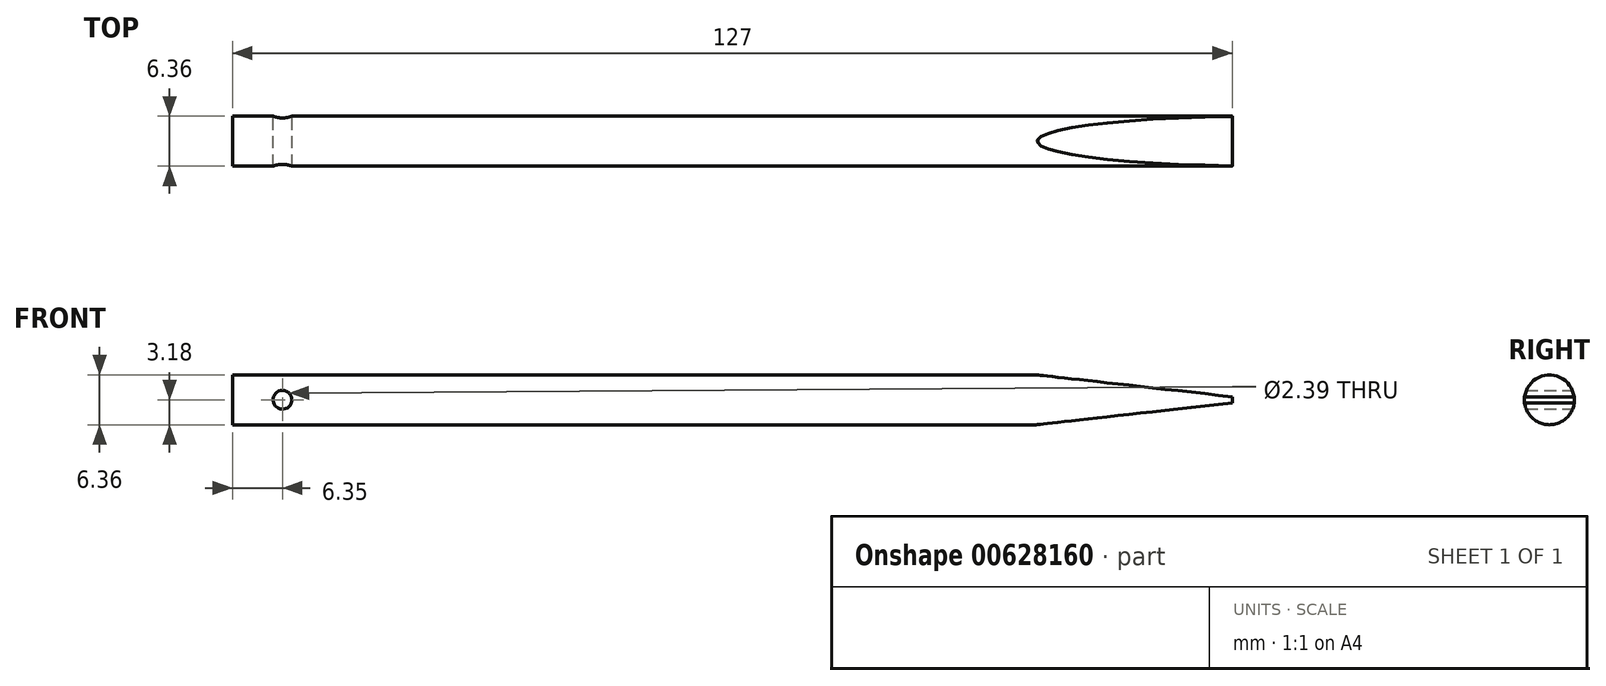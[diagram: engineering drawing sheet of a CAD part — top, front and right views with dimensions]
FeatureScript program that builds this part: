
annotation { "Feature Type Name" : "Feature", "Feature Type Description" : "" }
export const myFeature = defineFeature(function(context is Context, id is Id, definition is map)
    precondition{}
    {
        {
            var Q0;
            Q0=qCreatedBy(makeId("Right.planeOp"),FACE);
            var sketch = newSketch(context, id + "F0", { "sketchPlane" : qUnion([Q0])});
            skCircle(sketch, "E0", {"center": v(0, 0) * mm, "radius": 3.18 * mm});
            skSolve(sketch);
        }
        {
            var Q0;
            Q0 = qSketchRegion(id + "F0", true);
            extrude(context, id + "F1", {"entities" : qUnion([Q0]), "oppositeDirection" : true, "depth" : 127 * mm, "offsetDistance" : 25.4 * mm});
        }
        {
            var Q0;
            Q0=qCreatedBy(makeId("Front.planeOp"),FACE);
            var sketch = newSketch(context, id + "F2", { "sketchPlane" : qUnion([Q0])});
            skLineSegment(sketch, "E1", {"start": v(0, 0) * mm, "end": v(-25.4, 0) * mm, "construction": true});
            skLineSegment(sketch, "E2", {"start": v(0, 0) * mm, "end": v(0, 0.38) * mm});
            skLineSegment(sketch, "E3", {"start": v(-25.4, 3.23) * mm, "end": v(0, 0.38) * mm});
            skLineSegment(sketch, "E4.MirrorCS", {"start": v(0, 0) * mm, "end": v(0, -0.38) * mm});
            skLineSegment(sketch, "E5.MirrorCS", {"start": v(-25.4, -3.23) * mm, "end": v(0, -0.38) * mm});
            skLineSegment(sketch, "E6", {"start": v(-25.4, 3.23) * mm, "end": v(0, 3.23) * mm});
            skLineSegment(sketch, "E7", {"start": v(0, 3.23) * mm, "end": v(0, 0.38) * mm});
            skLineSegment(sketch, "E8", {"start": v(0, -0.38) * mm, "end": v(0, -3.21) * mm});
            skLineSegment(sketch, "E9", {"start": v(0, -3.21) * mm, "end": v(-25.4, -3.23) * mm});
            skSolve(sketch);
        }
        {
            var Q0;
            Q0=makeQuery(id+"F2.imprint","IMPRINT",FACE,{"disambiguationData":[TD([[makeQuery(id+"F2.imprint","IMPRINT",EDGE,{"derivedFrom":sQuery(id+"F2.wireOp",EDGE,"E3")}),1.0]])]});
            var Q1;
            Q1=makeQuery(id+"F2.imprint","IMPRINT",FACE,{"disambiguationData":[TD([[makeQuery(id+"F2.imprint","IMPRINT",EDGE,{"derivedFrom":sQuery(id+"F2.wireOp",EDGE,"E5.MirrorCS")}),-1.0]])]});
            extrude(context, id + "F3", {"entities" : qUnion([Q0, Q1]), "operationType" : NewBodyOperationType.REMOVE, "oppositeDirection" : true, "depth" : 25.4 * mm, "offsetDistance" : 25.4 * mm, "hasSecondDirection" : true, "secondDirectionOppositeDirection" : false, "secondDirectionDepth" : 25.4 * mm});
        }
        {
            var Q0;
            Q0=qCreatedBy(makeId("Front.planeOp"),FACE);
            var sketch = newSketch(context, id + "F4", { "sketchPlane" : qUnion([Q0])});
            skCircle(sketch, "E10", {"center": v(-120.65, 0) * mm, "radius": 1.2 * mm});
            skSolve(sketch);
        }
        {
            var Q0;
            Q0=sQuery(id+"F4.wireOp",EDGE,"E10");
            extrude(context, id + "F5", {"bodyType" : ToolBodyType.SURFACE, "surfaceEntities" : qUnion([Q0]), "depth" : 3.17 * mm, "offsetDistance" : 25.4 * mm, "hasSecondDirection" : true, "secondDirectionOppositeDirection" : true, "secondDirectionDepth" : 3.17 * mm});
        }
        {
            var Q0;
            Q0 = qSketchRegion(id + "F4", true);
            extrude(context, id + "F6", {"entities" : qUnion([Q0]), "operationType" : NewBodyOperationType.REMOVE, "depth" : 3.17 * mm, "offsetDistance" : 25.4 * mm, "hasSecondDirection" : true, "secondDirectionOppositeDirection" : true, "secondDirectionDepth" : 3.17 * mm});
        }
    });
